FCSTD DOCUMENT  (FreeCAD 0.21R33771 (Git))
Label: speaker v5
License: All rights reserved
LicenseURL: http://en.wikipedia.org/wiki/All_rights_reserved
objects: Sketcher::SketchObject×2, Spreadsheet::Sheet×1, PartDesign::Body×1, App::Part×1
note: 3 computed .brp shape members not serialized (recipe doc carries the construction recipe); baked Part::Feature solids carry a one-line shape summary decoded from their .brp

FEATURE [Spreadsheet::Sheet] Spreadsheet  label="Parameters"
  cells = A1='sp_thickness; B1(sp_thickness)=4; A2='sp_length; B2(sp_length)=500; A3='sp_height; B3(sp_height)=40; A4='ridge_height; B4=4; A5='ridge_width; B5=3; A6='ridge_sep; B6=3; A7='ridge_count; B7=4
FEATURE [Sketcher::SketchObject] Sketch
  FullyConstrained = true
  MapMode = 5
  Placement = pos=(0,0,0) rot=(0.57735,0.57735,0.57735;2.0944rad)
  Support = -> [YZ_Plane001]
  expr: Constraints[10] = <<Parameters>>.sp_thickness
  expr: Constraints[9] = <<Parameters>>.sp_height
  sketch-geometry (4):
    g0: LineSegment StartX=0 StartY=0 StartZ=0 EndX=4 EndY=0 EndZ=0
    g1: LineSegment StartX=4 StartY=0 StartZ=0 EndX=4 EndY=40 EndZ=0
    g2: LineSegment StartX=4 StartY=40 StartZ=0 EndX=0 EndY=40 EndZ=0
    g3: LineSegment StartX=0 StartY=40 StartZ=0 EndX=0 EndY=0 EndZ=0
  constraints (11):
    c: Coincident(g0,g1)
    c: Coincident(g1,g2)
    c: Coincident(g2,g3)
    c: Coincident(g3,g0)
    c: Horizontal(g0)
    c: Horizontal(g2)
    c: Vertical(g1)
    c: Vertical(g3)
    c: Coincident(g0,g-1)
    c: DistanceY(g1,g1) = 40
    c: DistanceX(g2,g2) = 4
FEATURE [Sketcher::SketchObject] Sketch001
  FullyConstrained = true
  MapMode = 5
  Placement = pos=(0,0,0) rot=(1,0,0;1.5708rad)
  Support = -> [XZ_Plane001]
  expr: Constraints[10] = <<Parameters>>.sp_thickness
  expr: Constraints[11] = <<Parameters>>.sp_thickness
  sketch-geometry (23):
    g0: LineSegment StartX=4 StartY=7 StartZ=0 EndX=8 EndY=7 EndZ=0
    g1: LineSegment StartX=8 StartY=7 StartZ=0 EndX=8 EndY=4 EndZ=0
    g2: LineSegment StartX=8 StartY=4 StartZ=0 EndX=4 EndY=4 EndZ=0
    g3: LineSegment StartX=4 StartY=4 StartZ=0 EndX=4 EndY=7 EndZ=0
    g4: ArcOfCircle CenterX=7.99999 CenterY=5.5 CenterZ=0 NormalX=0 NormalY=0 NormalZ=1 AngleXU=0 Radius=1.5 StartAngle=4.7124 EndAngle=7.85397
    g5: LineSegment StartX=4.1155 StartY=14.37 StartZ=0 EndX=8.1155 EndY=14.37 EndZ=0
    g6: LineSegment StartX=8.1155 StartY=14.37 StartZ=0 EndX=8.1155 EndY=11.37 EndZ=0
    g7: LineSegment StartX=8.1155 StartY=11.37 StartZ=0 EndX=4.1155 EndY=11.37 EndZ=0
    g8: LineSegment StartX=4.1155 StartY=11.37 StartZ=0 EndX=4.1155 EndY=14.37 EndZ=0
    g9: ArcOfCircle CenterX=8.11549 CenterY=12.87 CenterZ=0 NormalX=0 NormalY=0 NormalZ=1 AngleXU=0 Radius=1.5 StartAngle=4.7124 EndAngle=7.85397
    g10: LineSegment StartX=4 StartY=7 StartZ=0 EndX=4.1155 EndY=14.37 EndZ=0
    g11: LineSegment StartX=4.231 StartY=21.74 StartZ=0 EndX=8.231 EndY=21.74 EndZ=0
    g12: LineSegment StartX=8.231 StartY=21.74 StartZ=0 EndX=8.231 EndY=18.74 EndZ=0
    g13: LineSegment StartX=8.231 StartY=18.74 StartZ=0 EndX=4.231 EndY=18.74 EndZ=0
    g14: LineSegment StartX=4.231 StartY=18.74 StartZ=0 EndX=4.231 EndY=21.74 EndZ=0
    g15: ArcOfCircle CenterX=8.23099 CenterY=20.24 CenterZ=0 NormalX=0 NormalY=0 NormalZ=1 AngleXU=0 Radius=1.5 StartAngle=4.7124 EndAngle=7.85397
    g16: LineSegment StartX=4.1155 StartY=14.37 StartZ=0 EndX=4.231 EndY=21.74 EndZ=0
    g17: LineSegment StartX=4.3465 StartY=29.1101 StartZ=0 EndX=8.3465 EndY=29.1101 EndZ=0
    g18: LineSegment StartX=8.3465 StartY=29.1101 StartZ=0 EndX=8.3465 EndY=26.1101 EndZ=0
    g19: LineSegment StartX=8.3465 StartY=26.1101 StartZ=0 EndX=4.3465 EndY=26.1101 EndZ=0
    g20: LineSegment StartX=4.3465 StartY=26.1101 StartZ=0 EndX=4.3465 EndY=29.1101 EndZ=0
    g21: ArcOfCircle CenterX=8.34649 CenterY=27.6101 CenterZ=0 NormalX=0 NormalY=0 NormalZ=1 AngleXU=0 Radius=1.5 StartAngle=4.7124 EndAngle=7.85397
    g22: LineSegment StartX=4.231 StartY=21.74 StartZ=0 EndX=4.3465 EndY=29.1101 EndZ=0
  constraints (66):
    c: Coincident(g0,g1)
    c: Coincident(g1,g2)
    c: Coincident(g2,g3)
    c: Coincident(g3,g0)
    c: Horizontal(g0)
    c: Horizontal(g2)
    c: Vertical(g1)
    c: Vertical(g3)
    c: DistanceX(g0,g0) = 4
    c: DistanceY(g1,g1) = 3
    c: DistanceX(g-1,g2) = 4
    c: DistanceY(g-1,g1) = 4
    c: Coincident(g4,g0)
    c: Coincident(g4,g1)
    c: Radius(g4) = 1.5
    c: Coincident(g5,g6)
    c: Coincident(g6,g7)
    c: Coincident(g7,g8)
    c: Coincident(g8,g5)
    c: Horizontal(g5)
    c: Horizontal(g7)
    c: Vertical(g6)
    c: Vertical(g8)
    c: DistanceX(g5,g5) = 4
    c: DistanceY(g6,g6) = 3
    c: Coincident(g9,g5)
    c: Coincident(g9,g6)
    c: Radius(g9) = 1.5
    c: Coincident(g0,g10)
    c: Coincident(g5,g10)
    c: Distance(g10) = 7.37093
    c: Angle(g10) = 1.55513
    c: Coincident(g11,g12)
    c: Coincident(g12,g13)
    c: Coincident(g13,g14)
    c: Coincident(g14,g11)
    c: Horizontal(g11)
    c: Horizontal(g13)
    c: Vertical(g12)
    c: Vertical(g14)
    c: DistanceX(g11,g11) = 4
    c: DistanceY(g12,g12) = 3
    c: Coincident(g15,g11)
    c: Coincident(g15,g12)
    c: Radius(g15) = 1.5
    c: Coincident(g5,g16)
    c: Coincident(g11,g16)
    c: Equal(g10,g16)
    c: Parallel(g16,g10)
    c: Coincident(g17,g18)
    c: Coincident(g18,g19)
    c: Coincident(g19,g20)
    c: Coincident(g20,g17)
    c: Horizontal(g17)
    c: Horizontal(g19)
    c: Vertical(g18)
    c: Vertical(g20)
    c: DistanceX(g17,g17) = 4
    c: DistanceY(g18,g18) = 3
    c: Coincident(g21,g17)
    c: Coincident(g21,g18)
    c: Radius(g21) = 1.5
    c: Coincident(g11,g22)
    c: Coincident(g17,g22)
    c: Equal(g10,g22)
    c: Parallel(g22,g10)
FEATURE [PartDesign::Body] Body
  Group = -> [Sketch,Sketch001]
  Origin = -> Origin001
FEATURE [App::Part] Part  label="Side panel"
  Group = -> [Body]
  Origin = -> Origin
